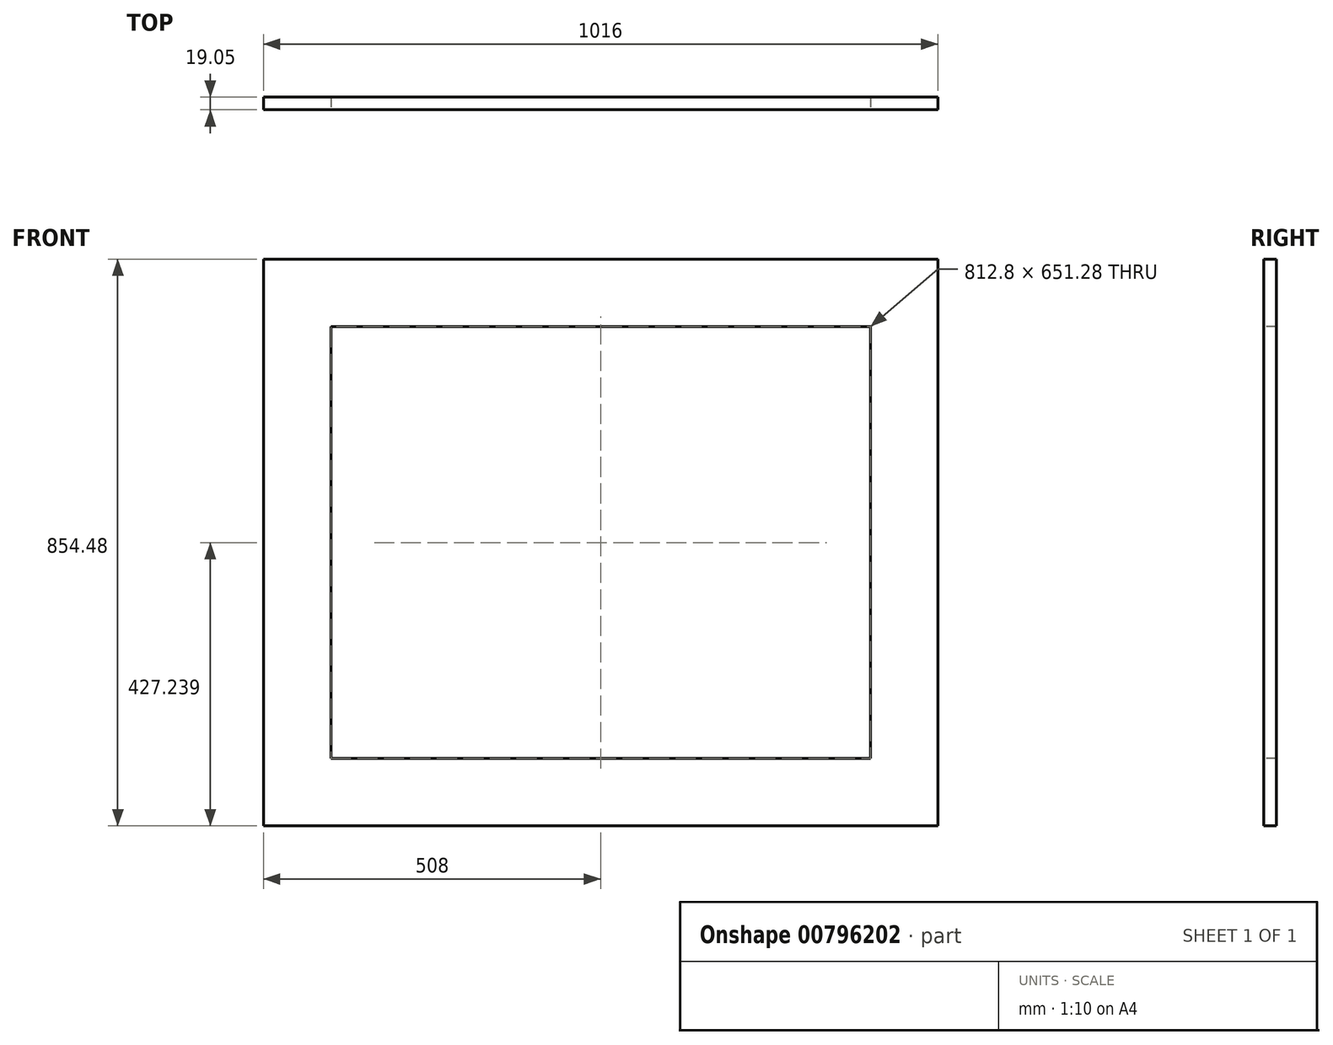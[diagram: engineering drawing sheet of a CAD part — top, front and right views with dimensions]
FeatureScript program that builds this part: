
annotation { "Feature Type Name" : "Feature", "Feature Type Description" : "" }
export const myFeature = defineFeature(function(context is Context, id is Id, definition is map)
    precondition{}
    {
        {
            var Q0;
            Q0=qCreatedBy(makeId("Front.planeOp"),FACE);
            var sketch = newSketch(context, id + "F0", { "sketchPlane" : qUnion([Q0])});
            skLineSegment(sketch, "E0.bottom", {"start": v(0, 0) * mm, "end": v(1016, 0) * mm});
            skLineSegment(sketch, "E0.top", {"start": v(0, -854.48) * mm, "end": v(1016, -854.48) * mm});
            skLineSegment(sketch, "E0.left", {"start": v(0, 0) * mm, "end": v(0, -854.48) * mm});
            skLineSegment(sketch, "E0.right", {"start": v(1016, 0) * mm, "end": v(1016, -854.48) * mm});
            skSolve(sketch);
        }
        {
            var Q0;
            Q0=makeQuery(id+"F0.imprint","IMPRINT",FACE,{"disambiguationData":[TD([[makeQuery(id+"F0.imprint","IMPRINT",EDGE,{"derivedFrom":sQuery(id+"F0.wireOp",EDGE,"E0.bottom")}),-1.0]])]});
            extrude(context, id + "F1", {"entities" : qUnion([Q0]), "depth" : 19.05 * mm, "offsetDistance" : 25.4 * mm});
        }
        {
            var Q0;
            Q0=makeQuery(id+"F1.opExtrude","CAP_FACE",FACE,{"disambiguationData":[OSD([sQuery(id+"F0.wireOp",EDGE,"E0.bottom"),sQuery(id+"F0.wireOp",EDGE,"E0.top"),sQuery(id+"F0.wireOp",EDGE,"E0.left"),sQuery(id+"F0.wireOp",EDGE,"E0.right")])],"isStart":false});
            var sketch = newSketch(context, id + "F2", { "sketchPlane" : qUnion([Q0])});
            skLineSegment(sketch, "E1.bottom", {"start": v(101.6, -101.6) * mm, "end": v(914.4, -101.6) * mm});
            skLineSegment(sketch, "E1.top", {"start": v(101.6, -752.88) * mm, "end": v(914.4, -752.88) * mm});
            skLineSegment(sketch, "E1.left", {"start": v(101.6, -101.6) * mm, "end": v(101.6, -752.88) * mm});
            skLineSegment(sketch, "E1.right", {"start": v(914.4, -101.6) * mm, "end": v(914.4, -752.88) * mm});
            skSolve(sketch);
        }
        {
            var Q0;
            Q0=makeQuery(id+"F2.imprint","IMPRINT",FACE,{"disambiguationData":[TD([[makeQuery(id+"F2.imprint","IMPRINT",EDGE,{"derivedFrom":sQuery(id+"F2.wireOp",EDGE,"E1.bottom")}),-1.0]])]});
            var Q1;
            Q1 = qConstructionFilter(qBodyType(qCreatedBy(id + "F2" ,EDGE), BodyType.WIRE), ConstructionObject.NO);
            extrude(context, id + "F3", {"entities" : qUnion([Q0]), "operationType" : NewBodyOperationType.REMOVE, "surfaceEntities" : qUnion([Q1]), "endBound" : BoundingType.THROUGH_ALL, "oppositeDirection" : true, "depth" : 25.4 * mm, "offsetDistance" : 25.4 * mm});
        }
    });
